# Revit family: Faucet-Wall_Mount-Bath-KOHLER-LOURE-K-14712T_1
name_source: partatom
category: Plumbing Fixtures
revit_build: Autodesk Revit 2017 (Build: 20160225_1515(x64)
units: mm (PartAtom-declared; Revit-internal decimal feet)

## family parameters
Cut with Voids When Loaded = No
Host = Face
OmniClass Number = 23.31.11.00
OmniClass Title = Faucets
Part Type = Normal
Room Calculation Point = No
Round Connector Dimension = Use Diameter
Shared = No

## types (4) — shared parameters
ADA Compliant = No
Assembly Code = D2010
CW Connection = Yes
Cold Water Inlet = Cold Water Inlet
Date Modified = 09/28/2020
Default Elevation = 36"
Description = RECE. DUAL HANDLE BATH FAUCET
Drain Included = No
Flow Rate = 0 GPM
HW Connection = Yes
Handle Clearance = 2 5/8"
Handle Height = 1 5/16"
Height = 9 3/16"
Hot Water Inlet = Hot Water Inlet
Length = 2"
Manufacturer = KOHLER Co.
Master Format 2014 = 22 41 39
Master Format 2014 Name = Residential Faucets, Supplies, and Trim
Material = Solid Metal Construction
Pressure = 0.00 psi
Product Documentation Link = https://files.kohler.com.cn
Product Name = LOURE
Spout Reach = 2"
URL = http://www.kohler.com.cn
Vent Connection = No
Waste Connection = No
Waste Water Outlet = Waste Water Outlet
WaterSense Certified = No

## per-type parameters (varying)
| type | Finish | Model | Product Page URL | Type |
| CP-Polished Chrome | Kohler-Metal-CP-Polished_Chrome | K-14712T-4-CP | https://www.kohler.com.cn | 1 |
| BL-Matte Black | Kohler-Metal-BL-Matte_Black | K-14712T-4-BL |  | 2 |
| BV-Romen Copper | Kohler-Metal-BV-Roman_Copper | K-14712T-4-BV |  | 3 |
| SN-Champagne Gold | Kohler-Metal-SN-Champagne_Gold | K-14712T-4-SN |  | 4 |

## geometry (parser evidence)
native form markers: Sweep x11
no freeform markers — native parametric forms only
